# Revit family: Injektionssystem VMU plus, VA
name_source: partatom
category: HLS-Bauteile
revit_build: Autodesk Revit 2017 (Build: 20190507_1515(x64)
units: mm (PartAtom-declared; Revit-internal decimal feet)

## family parameters
Basisbauteil = Fläche
Beim Laden mit Abzugskörper schneiden = Nein
Bemaßung runder Anschluss = Durchmesser verwenden
Gemeinsam genutzt = Ja
Raumberechnungspunkt = Nein
Teiletyp = Normal

## types (6) — shared parameters
Anwendungsbereich = Beton und Mauerwerk
Bohrlochtiefe (Beton) = 110 mm
Brandschutz = ja
Fabrikat = MKT
Festigkeitsklasse = 5.8
Firma = MEFA Befestigungs- und Montagesysteme GmbH
Material = Edelstahl
Mengeneinheit = St
Oberflaeche = Edelstahl
Vorgabe-Ansicht = 1219 mm
vpe = 10 St

## per-type parameters (varying)
- Ankerstange VMU-A M16x160, VA4: Artikelnummer=222831810501; Bohrerdurchmesser (Beton)=18 mm; Bohrerdurchmesser (Vollstein)=18 mm; Bohrlochtiefe (Vollstein)=100 mm; D=14 mm  [stored 0.0459318 ft]; EAN=4250928457745; Gewicht=0.27 kg; Gewicht pro Bauteil=0.27 kg; Gewinde=M16; Kurztext1=Ankerstange VMU plus A M16 V4A; Kurztext2=Länge 160 mm; L=160 mm  [stored 0.524934 ft]; L1=140 mm  [stored 0.459318 ft]; L2=20 mm  [stored 0.0656168 ft]; Länge=160 mm  [stored 0.524934 ft]; Länge Dübel=160 mm  [stored 0.524934 ft]; Mutter=Sechskantmutter : Sechskantmutter M16; Schlüsselweite=24; Unterlegscheibe=Unterlegscheibe : Unterlegscheibe, verstärkt 17x44x3.5; max. Klemmstärke (Beton)=15 mm; max. Klemmstärke (Vollstein)=40 mm; max. Klemmstärke bei Siebhülse 20x130=10 mm; max. Klemmstärke bei Siebhülse 20x85=55 mm
- Ankerstange VMU-A M 8x130, VA4: Artikelnummer=222831525501; Bohrerdurchmesser (Beton)=10 mm; Bohrerdurchmesser (Vollstein)=10 mm; Bohrlochtiefe (Vollstein)=80 mm; D=7 mm  [stored 0.0229659 ft]; EAN=4043315065155; Gewicht=0.05 kg; Gewicht pro Bauteil=0.05 kg; Gewinde=M8; Kurztext1=Ankerstange VMU plus A M8 V4A; Kurztext2=Länge 130 mm; L=130 mm  [stored 0.426509 ft]; L1=115 mm  [stored 0.377297 ft]; L2=15 mm  [stored 0.0492126 ft]; Länge=130 mm  [stored 0.426509 ft]; Länge Dübel=130 mm  [stored 0.426509 ft]; Mutter=Sechskantmutter : Sechskantmutter M8; Schlüsselweite=13; Unterlegscheibe=Unterlegscheibe : Unterlegscheibe 8.4x16x1.6; max. Klemmstärke (Beton)=40 mm; max. Klemmstärke (Vollstein)=40 mm; max. Klemmstärke bei Siebhülse 16x85=35 mm
- Ankerstange VMU-A M10x130, VA4: Artikelnummer=222831625501; Bohrerdurchmesser (Beton)=12 mm; Bohrerdurchmesser (Vollstein)=12 mm; Bohrlochtiefe (Vollstein)=90 mm; D=8 mm  [stored 0.0262467 ft]; EAN=4043315064479; Gewicht=0.09 kg; Gewicht pro Bauteil=0.09 kg; Gewinde=M10; Kurztext1=Ankerstange VMU plus A M10 V4A; Kurztext2=Länge 130 mm; L=130 mm  [stored 0.426509 ft]; L1=115 mm  [stored 0.377297 ft]; L2=15 mm  [stored 0.0492126 ft]; Länge=130 mm  [stored 0.426509 ft]; Länge Dübel=130 mm  [stored 0.426509 ft]; Mutter=Sechskantmutter : Sechskantmutter M10; Schlüsselweite=17; Unterlegscheibe=Unterlegscheibe : Unterlegscheibe 10.5x20x2; max. Klemmstärke (Beton)=30 mm; max. Klemmstärke (Vollstein)=30 mm; max. Klemmstärke bei Siebhülse 16x85=35 mm
- Ankerstange VMU-A M10x165, VA4: Artikelnummer=222831635501; Bohrerdurchmesser (Beton)=12 mm; Bohrerdurchmesser (Vollstein)=12 mm; Bohrlochtiefe (Vollstein)=90 mm; D=8 mm  [stored 0.0262467 ft]; EAN=4043315064530; Gewicht=0.10 kg; Gewicht pro Bauteil=0.10 kg; Gewinde=M10; Kurztext1=Ankerstange VMU plus A M10 V4A; Kurztext2=Länge 165 mm; L=165 mm  [stored 0.541339 ft]; L1=150 mm; L2=15 mm  [stored 0.0492126 ft]; Länge=165 mm  [stored 0.541339 ft]; Länge Dübel=165 mm  [stored 0.541339 ft]; Mutter=Sechskantmutter : Sechskantmutter M10; Schlüsselweite=17; Unterlegscheibe=Unterlegscheibe : Unterlegscheibe 10.5x20x2; max. Klemmstärke (Beton)=65 mm; max. Klemmstärke (Vollstein)=65 mm; max. Klemmstärke bei Siebhülse 16x130=25 mm; max. Klemmstärke bei Siebhülse 16x85=70 mm
- Ankerstange VMU-A M12x155, VA4: Artikelnummer=222831720501; Bohrerdurchmesser (Beton)=14 mm; Bohrerdurchmesser (Vollstein)=14 mm; Bohrlochtiefe (Vollstein)=90 mm; D=10 mm  [stored 0.0328084 ft]; EAN=4043315064660; Gewicht=0.14 kg; Gewicht pro Bauteil=0.14 kg; Gewinde=M12; Kurztext1=Ankerstange VMU plus A M12 V4A; Kurztext2=Länge 155 mm; L=155 mm  [stored 0.50853 ft]; L1=140 mm  [stored 0.459318 ft]; L2=15 mm  [stored 0.0492126 ft]; Länge=155 mm  [stored 0.50853 ft]; Länge Dübel=155 mm  [stored 0.50853 ft]; Mutter=Sechskantmutter : Sechskantmutter M12; Schlüsselweite=19; Unterlegscheibe=Unterlegscheibe : Unterlegscheibe 13x24x2.5; max. Klemmstärke (Beton)=30 mm; max. Klemmstärke (Vollstein)=40 mm; max. Klemmstärke bei Siebhülse 20x130=10 mm; max. Klemmstärke bei Siebhülse 20x85=55 mm
- Ankerstange VMU-A M12x210, VA4: Artikelnummer=222831740501; Bohrerdurchmesser (Beton)=14 mm; Bohrerdurchmesser (Vollstein)=14 mm; Bohrlochtiefe (Vollstein)=90 mm; D=10 mm  [stored 0.0328084 ft]; EAN=4043315064721; Gewicht=0.18 kg; Gewicht pro Bauteil=0.18 kg; Gewinde=M12; Kurztext1=Ankerstange VMU plus A M12 V4A; Kurztext2=Länge 210 mm; L=210 mm  [stored 0.688976 ft]; L1=195 mm  [stored 0.639764 ft]; L2=15 mm  [stored 0.0492126 ft]; Länge=210 mm  [stored 0.688976 ft]; Länge Dübel=210 mm  [stored 0.688976 ft]; Mutter=Sechskantmutter : Sechskantmutter M12; Schlüsselweite=19; Unterlegscheibe=Unterlegscheibe : Unterlegscheibe 13x24x2.5; max. Klemmstärke (Beton)=85 mm; max. Klemmstärke (Vollstein)=95 mm; max. Klemmstärke bei Siebhülse 20x130=65 mm; max. Klemmstärke bei Siebhülse 20x85=110 mm

note: [stored X ft] marks values corroborated as IEEE doubles in the binary element streams (Revit-internal decimal feet)

## geometry (parser evidence)
native form markers: Sweep x2
no freeform markers — native parametric forms only
